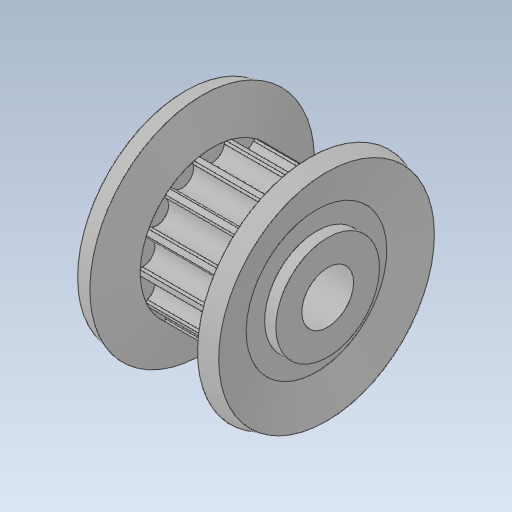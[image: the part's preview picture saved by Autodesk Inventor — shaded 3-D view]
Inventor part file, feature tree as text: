
AUTODESK INVENTOR PART (.ipt)
format: ipt  version: 2024 (Build 280153000, 153)  size: 287,744 bytes
history: native  units: mm
features: sketch x5, revolve x3, extrude x1, pattern_circular x1, hole x1
ambient origin geometry x8: Origin, YZ Plane, XZ Plane, XY Plane, X Axis, Y Axis, Z Axis, Center Point
bodies: Solid1 (feature_tree)
feature tree (11):
  revolve  "Revolution1"  [1 undecoded]
  extrude  "Extrusion1"  TaperAngle=360.0deg  [1 undecoded]
  pattern_circular  "Circular Pattern1"  [2 undecoded]
  revolve  "Revolution2"  [1 undecoded]
  revolve  "Revolution3"  [1 undecoded]
  hole  "Hole1"  [1 undecoded]
  sketch  "Sketch_16"  dims[d3=140.0mm d4=4.48799mm d6=360.0deg]
  sketch  "Sketch_18"  dims[d7=360.0deg]
  sketch  "Sketch_20"  dims[d8=3.0mm d9=6.0mm d10=4.0mm d11=2.0mm d12=90.0deg d13=8.3mm d14=0.0mm]
  sketch  "Sketch_21"
  sketch  "Sketch5"  dims[d0=360.0deg d1=5.0mm d2=0.0mm]
note: 7 required parameter values undecoded (feature->parameter linkage not recoverable at this tier; creation-order binding heuristic only, values carry confidence <= 0.55)